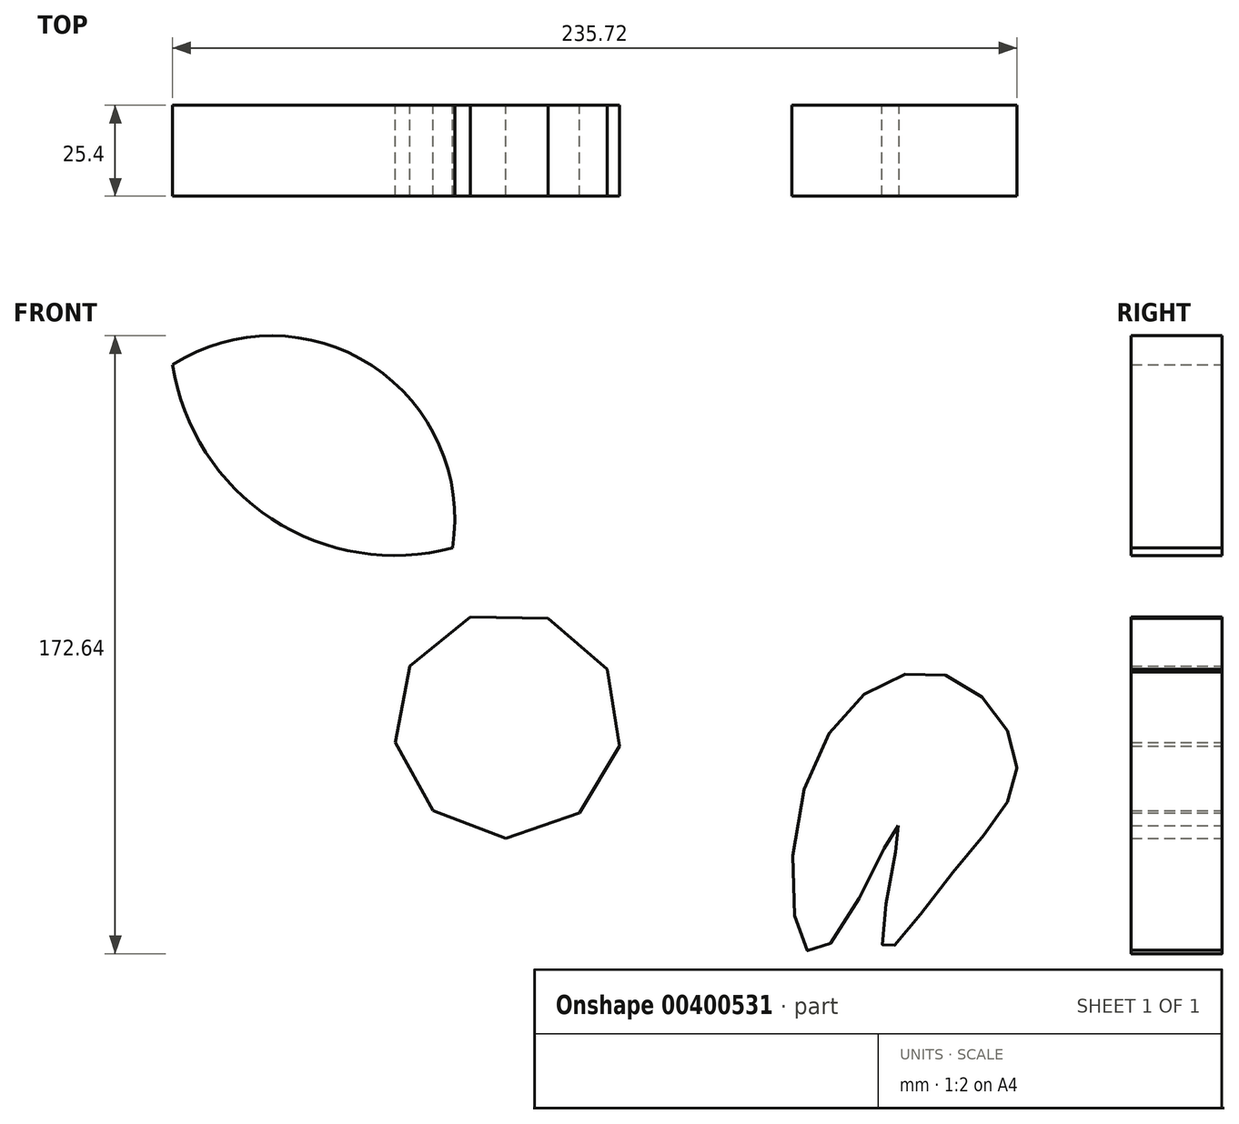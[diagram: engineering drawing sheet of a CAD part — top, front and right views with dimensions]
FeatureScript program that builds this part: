
annotation { "Feature Type Name" : "Feature", "Feature Type Description" : "" }
export const myFeature = defineFeature(function(context is Context, id is Id, definition is map)
    precondition{}
    {
        {
            var Q0;
            Q0=qCreatedBy(makeId("Front.planeOp"),FACE);
            var sketch = newSketch(context, id + "F0", { "sketchPlane" : qUnion([Q0])});
            skCircle(sketch, "E0.cCircle", {"center": v(0, 4.86) * mm, "radius": 29.88 * mm, "construction": true});
            skLineSegment(sketch, "E0.0", {"start": v(-31.4, -0.16) * mm, "end": v(-27.28, 21.2) * mm});
            skLineSegment(sketch, "E0.1", {"start": v(-27.28, 21.2) * mm, "end": v(-10.4, 34.91) * mm});
            skLineSegment(sketch, "E0.2", {"start": v(-10.4, 34.91) * mm, "end": v(11.36, 34.56) * mm});
            skLineSegment(sketch, "E0.3", {"start": v(11.36, 34.56) * mm, "end": v(27.8, 20.31) * mm});
            skLineSegment(sketch, "E0.4", {"start": v(27.8, 20.31) * mm, "end": v(31.22, -1.17) * mm});
            skLineSegment(sketch, "E0.5", {"start": v(31.22, -1.17) * mm, "end": v(20.04, -19.83) * mm});
            skLineSegment(sketch, "E0.6", {"start": v(20.04, -19.83) * mm, "end": v(-0.51, -26.94) * mm});
            skLineSegment(sketch, "E0.7", {"start": v(-0.51, -26.94) * mm, "end": v(-20.83, -19.17) * mm});
            skLineSegment(sketch, "E0.8", {"start": v(-20.83, -19.17) * mm, "end": v(-31.4, -0.16) * mm});
            skPoint(sketch, "E0.0.midPoint", {"position": v(-29.34, 10.52) * mm});
            skFitSpline(sketch, "E1", {"points": [v(109.09, -23.38) * mm, v(87.03, -58.88) * mm, v(83.58, -10.75) * mm, v(120.2, 19.15) * mm, v(142.16, -6.12) * mm, v(123.16, -37.88) * mm, v(104.75, -57.33) * mm, v(109.09, -23.38) * mm]});
            skCircle(sketch, "E2", {"center": v(-31.57, 114.75) * mm, "radius": 62.68 * mm});
            skCircle(sketch, "E3", {"center": v(-65.9, 62.32) * mm, "radius": 51.15 * mm});
            skCircle(sketch, "E4", {"center": v(-97.45, 22.05) * mm, "radius": 43.15 * mm});
            skCircle(sketch, "E5", {"center": v(-115.99, -16.9) * mm, "radius": 37.3 * mm});
            skCircle(sketch, "E6", {"center": v(-125.44, -53) * mm, "radius": 29.44 * mm});
            skCircle(sketch, "E7", {"center": v(-132.29, -81.63) * mm, "radius": 24.01 * mm});
            skCircle(sketch, "E8", {"center": v(-133.71, -105.6) * mm, "radius": 19.17 * mm});
            skSolve(sketch);
        }
        {
            var Q0;
            Q0=makeQuery(id+"F0.imprint","IMPRINT",FACE,{"disambiguationData":[TD([[makeQuery(id+"F0.imprint","IMPRINT",EDGE,{"derivedFrom":sQuery(id+"F0.wireOp",EDGE,"E0.0")}),-1.0]])]});
            var Q1;
            {var subQ0=sQuery(id+"F0.wireOp",EDGE,"E3");var subQ1=sQuery(id+"F0.wireOp",EDGE,"E2");var subQ2=makeQuery(id+"F0.imprint","INTERSECT",VERTEX,{"disambiguationData":[OD(0.0)],"derivedFrom":[subQ1,subQ0]});Q1=makeQuery(id+"F0.imprint","IMPRINT",FACE,{"disambiguationData":[TD([[makeQuery(id+"F0.imprint","IMPRINT",EDGE,{"disambiguationData":[TD([[subQ2,1.0]])],"derivedFrom":subQ1}),1.0]])]});}
            var Q2;
            {var subQ0=sQuery(id+"F0.wireOp",EDGE,"E4");var subQ1=sQuery(id+"F0.wireOp",EDGE,"E3");var subQ2=makeQuery(id+"F0.imprint","INTERSECT",VERTEX,{"disambiguationData":[OD(0.0)],"derivedFrom":[subQ1,subQ0]});Q2=makeQuery(id+"F0.imprint","IMPRINT",FACE,{"disambiguationData":[TD([[makeQuery(id+"F0.imprint","IMPRINT",EDGE,{"disambiguationData":[TD([[subQ2,-1.0]])],"derivedFrom":subQ1}),-1.0]])]});}
            var Q3;
            {var subQ0=sQuery(id+"F0.wireOp",EDGE,"E8");var subQ1=sQuery(id+"F0.wireOp",EDGE,"E7");var subQ2=makeQuery(id+"F0.imprint","INTERSECT",VERTEX,{"disambiguationData":[OD(0.0)],"derivedFrom":[subQ1,subQ0]});Q3=makeQuery(id+"F0.imprint","IMPRINT",FACE,{"disambiguationData":[TD([[makeQuery(id+"F0.imprint","IMPRINT",EDGE,{"disambiguationData":[TD([[subQ2,-1.0]])],"derivedFrom":subQ1}),-1.0]])]});}
            var Q4;
            Q4=makeQuery(id+"F0.imprint","IMPRINT",FACE,{"disambiguationData":[TD([[makeQuery(id+"F0.imprint","IMPRINT",EDGE,{"derivedFrom":sQuery(id+"F0.wireOp",EDGE,"E1")}),-1.0]])]});
            extrude(context, id + "F1", {"entities" : qUnion([Q0, Q1, Q2, Q3, Q4]), "depth" : 25.4 * mm});
        }
    });
